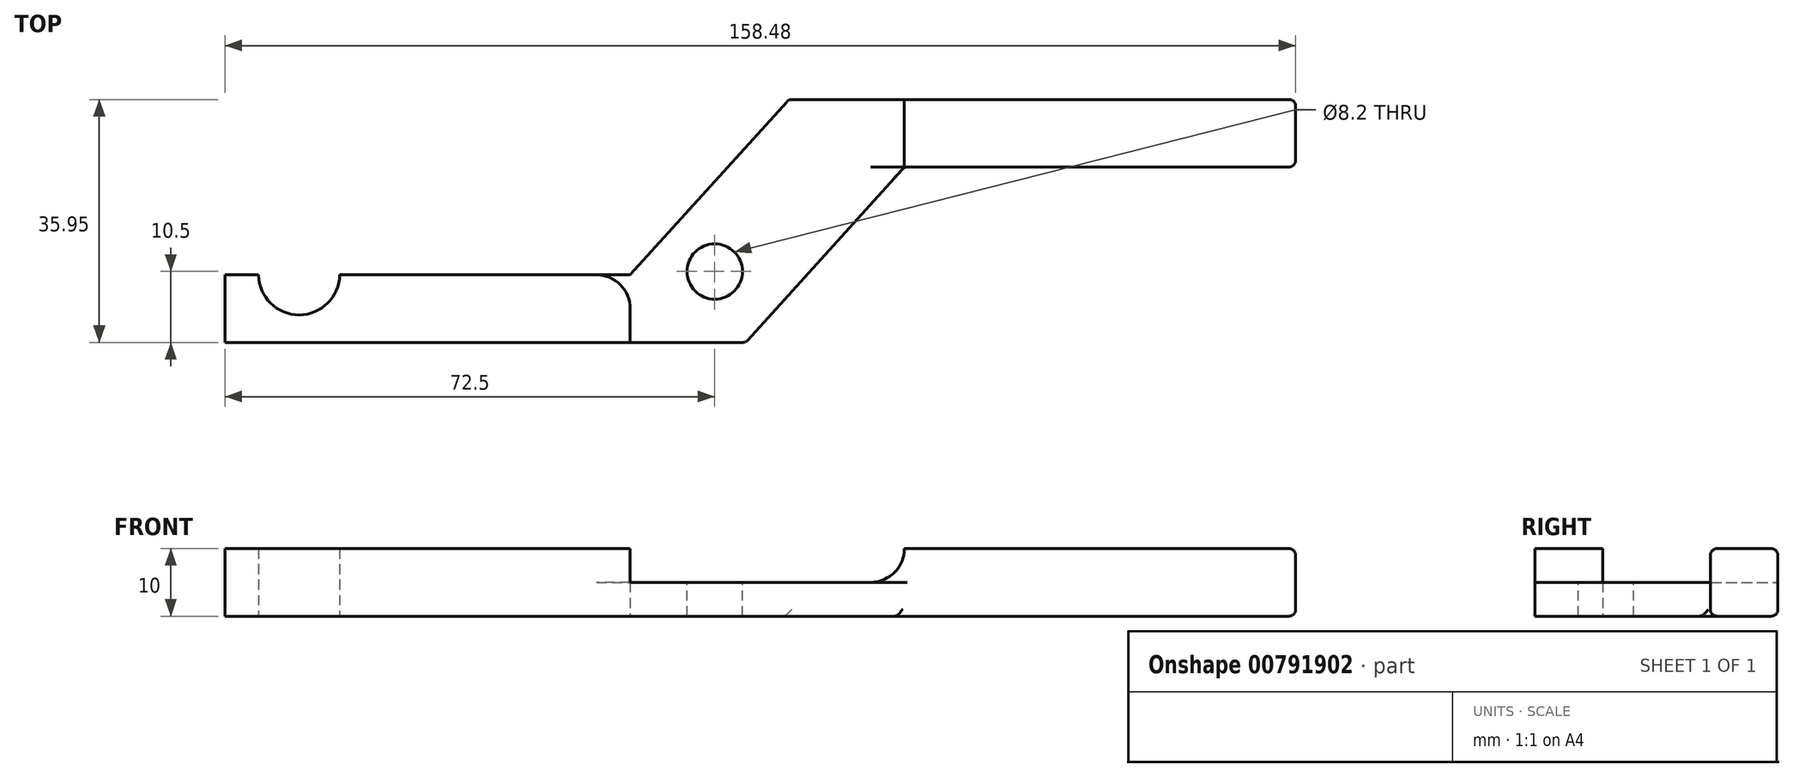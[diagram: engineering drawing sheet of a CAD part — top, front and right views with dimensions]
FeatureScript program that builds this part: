
annotation { "Feature Type Name" : "Feature", "Feature Type Description" : "" }
export const myFeature = defineFeature(function(context is Context, id is Id, definition is map)
    precondition{}
    {
        {
            var Q0;
            Q0=qCreatedBy(makeId("Top.planeOp"),FACE);
            var sketch = newSketch(context, id + "F0", { "sketchPlane" : qUnion([Q0])});
            skLineSegment(sketch, "E0", {"start": v(0, 0) * mm, "end": v(-43, 0) * mm});
            skLineSegment(sketch, "E1", {"start": v(0, 0) * mm, "end": v(23.48, 25.95) * mm});
            skLineSegment(sketch, "E2", {"start": v(23.48, 25.95) * mm, "end": v(98.48, 25.95) * mm});
            skArc(sketch, "E3", {"start": v(-55, 0) * mm, "mid": v(-49, -5.92) * mm, "end": v(-43, 0) * mm});
            skLineSegment(sketch, "E4", {"start": v(-60, 0) * mm, "end": v(-60, -10) * mm});
            skLineSegment(sketch, "E5", {"start": v(-60, -10) * mm, "end": v(17.09, -10) * mm});
            skLineSegment(sketch, "E6", {"start": v(17.09, -10) * mm, "end": v(40.57, 15.95) * mm});
            skLineSegment(sketch, "E7", {"start": v(40.57, 15.95) * mm, "end": v(98.48, 15.95) * mm});
            skLineSegment(sketch, "E8", {"start": v(98.48, 15.95) * mm, "end": v(98.48, 25.95) * mm});
            skLineSegment(sketch, "E9.trimOffspring", {"start": v(-55, 0) * mm, "end": v(-60, 0) * mm});
            skSolve(sketch);
        }
        {
            var Q0;
            Q0=qSketchRegion(id+"F0",true);
            extrude(context, id + "F1", {"entities" : qUnion([Q0]), "depth" : 10 * mm, "offsetDistance" : 25 * mm});
        }
        {
            var Q0;
            Q0=makeQuery(id+"F1.opExtrude","CAP_FACE",FACE,{"disambiguationData":[OSD([sQuery(id+"F0.wireOp",EDGE,"E0"),sQuery(id+"F0.wireOp",EDGE,"E1"),sQuery(id+"F0.wireOp",EDGE,"E2"),sQuery(id+"F0.wireOp",EDGE,"E3"),sQuery(id+"F0.wireOp",EDGE,"E4"),sQuery(id+"F0.wireOp",EDGE,"E5"),sQuery(id+"F0.wireOp",EDGE,"E6"),sQuery(id+"F0.wireOp",EDGE,"E7"),sQuery(id+"F0.wireOp",EDGE,"E8"),sQuery(id+"F0.wireOp",EDGE,"E9.trimOffspring")])],"isStart":false});
            var sketch = newSketch(context, id + "F2", { "sketchPlane" : qUnion([Q0])});
            skLineSegment(sketch, "E10", {"start": v(17.09, -10) * mm, "end": v(40.57, 15.95) * mm});
            skLineSegment(sketch, "E11", {"start": v(23.48, 25.95) * mm, "end": v(0, 0) * mm});
            skCircle(sketch, "E12", {"center": v(12.5, 0.5) * mm, "radius": 4.1 * mm});
            skLineSegment(sketch, "E13", {"start": v(0, 0) * mm, "end": v(0, -10) * mm});
            skLineSegment(sketch, "E14", {"start": v(0, -10) * mm, "end": v(17.09, -10) * mm});
            skLineSegment(sketch, "E15", {"start": v(40.57, 15.95) * mm, "end": v(40.57, 25.95) * mm});
            skLineSegment(sketch, "E16", {"start": v(40.57, 25.95) * mm, "end": v(23.48, 25.95) * mm});
            skSolve(sketch);
        }
        {
            var Q0;
            Q0 = qSketchRegion(id + "F2", true);
            extrude(context, id + "F3", {"entities" : qUnion([Q0]), "operationType" : NewBodyOperationType.REMOVE, "oppositeDirection" : true, "depth" : 5 * mm, "offsetDistance" : 25 * mm});
        }
        {
            var Q0;
            Q0=makeQuery(id+"F3.boolean.opBoolean","SPLIT",FACE,{"disambiguationData":[TD([makeQuery(id+"F3.opExtrude","SWEPT_FACE",FACE,{"disambiguationData":[OSD([sQuery(id+"F2.wireOp",EDGE,"E12")])]})])],"derivedFrom":makeQuery(id+"F1.opExtrude","CAP_FACE",FACE,{"disambiguationData":[OSD([sQuery(id+"F0.wireOp",EDGE,"E0"),sQuery(id+"F0.wireOp",EDGE,"E1"),sQuery(id+"F0.wireOp",EDGE,"E2"),sQuery(id+"F0.wireOp",EDGE,"E3"),sQuery(id+"F0.wireOp",EDGE,"E4"),sQuery(id+"F0.wireOp",EDGE,"E5"),sQuery(id+"F0.wireOp",EDGE,"E6"),sQuery(id+"F0.wireOp",EDGE,"E7"),sQuery(id+"F0.wireOp",EDGE,"E8"),sQuery(id+"F0.wireOp",EDGE,"E9.trimOffspring")])],"isStart":false})});
            var Q1;
            Q1=makeQuery(id+"F1.opExtrude","CAP_FACE",FACE,{"disambiguationData":[OSD([sQuery(id+"F0.wireOp",EDGE,"E0"),sQuery(id+"F0.wireOp",EDGE,"E1"),sQuery(id+"F0.wireOp",EDGE,"E2"),sQuery(id+"F0.wireOp",EDGE,"E3"),sQuery(id+"F0.wireOp",EDGE,"E4"),sQuery(id+"F0.wireOp",EDGE,"E5"),sQuery(id+"F0.wireOp",EDGE,"E6"),sQuery(id+"F0.wireOp",EDGE,"E7"),sQuery(id+"F0.wireOp",EDGE,"E8"),sQuery(id+"F0.wireOp",EDGE,"E9.trimOffspring")])],"isStart":true});
            extrude(context, id + "F4", {"entities" : qUnion([Q0]), "operationType" : NewBodyOperationType.REMOVE, "endBound" : BoundingType.UP_TO_SURFACE, "oppositeDirection" : true, "depth" : 25 * mm, "endBoundEntityFace" : qUnion([Q1]), "offsetDistance" : 25 * mm});
        }
        {
            var Q0;
            Q0=makeQuery(id+"F1.opExtrude","CAP_EDGE",EDGE,{"disambiguationData":[OSD([sQuery(id+"F0.wireOp",EDGE,"E2")])],"isStart":true});
            var Q1;
            Q1=makeQuery(id+"F1.opExtrude","CAP_EDGE",EDGE,{"disambiguationData":[OSD([sQuery(id+"F0.wireOp",EDGE,"E2")])],"isStart":false});
            var Q2;
            Q2=makeQuery(id+"F1.opExtrude","SWEPT_EDGE",EDGE,{"disambiguationData":[OSD([sQuery(id+"F0.wireOp",EDGE,"E2"),sQuery(id+"F0.wireOp",EDGE,"E8")])]});
            var Q3;
            Q3=makeQuery(id+"F1.opExtrude","CAP_EDGE",EDGE,{"disambiguationData":[OSD([sQuery(id+"F0.wireOp",EDGE,"E8")])],"isStart":true});
            var Q4;
            Q4=makeQuery(id+"F1.opExtrude","CAP_EDGE",EDGE,{"disambiguationData":[OSD([sQuery(id+"F0.wireOp",EDGE,"E8")])],"isStart":false});
            var Q5;
            Q5=makeQuery(id+"F1.opExtrude","SWEPT_EDGE",EDGE,{"disambiguationData":[OSD([sQuery(id+"F0.wireOp",EDGE,"E7"),sQuery(id+"F0.wireOp",EDGE,"E8")])]});
            var Q6;
            Q6=makeQuery(id+"F1.opExtrude","CAP_EDGE",EDGE,{"disambiguationData":[OSD([sQuery(id+"F0.wireOp",EDGE,"E7")])],"isStart":true});
            var Q7;
            Q7=makeQuery(id+"F1.opExtrude","CAP_EDGE",EDGE,{"disambiguationData":[OSD([sQuery(id+"F0.wireOp",EDGE,"E7")])],"isStart":false});
            var Q8;
            Q8=makeQuery(id+"F1.opExtrude","SWEPT_EDGE",EDGE,{"disambiguationData":[OSD([sQuery(id+"F0.wireOp",EDGE,"E1"),sQuery(id+"F0.wireOp",EDGE,"E2")])]});
            var Q9;
            Q9=makeQuery(id+"F1.opExtrude","SWEPT_EDGE",EDGE,{"disambiguationData":[OSD([sQuery(id+"F0.wireOp",EDGE,"E5"),sQuery(id+"F0.wireOp",EDGE,"E6")])]});
            var Q10;
            Q10=makeQuery(id+"F3.boolean.opBoolean","SPLIT",EDGE,{"derivedFrom":makeQuery(id+"F1.opExtrude","SWEPT_EDGE",EDGE,{"disambiguationData":[OSD([sQuery(id+"F0.wireOp",EDGE,"E6"),sQuery(id+"F0.wireOp",EDGE,"E7")])]})});
            fillet(context, id + "F5", {"entities" : qUnion([Q0, Q1, Q2, Q3, Q4, Q5, Q6, Q7, Q8, Q9, Q10]), "radius" : 1 * mm, "tangentPropagation" : true, "allowEdgeOverflow" : false});
        }
        {
            var Q0;
            Q0=makeQuery(id+"F3.boolean.opBoolean","COPY",EDGE,{"derivedFrom":makeQuery(id+"F3.opExtrude","CAP_EDGE",EDGE,{"disambiguationData":[OSD([sQuery(id+"F2.wireOp",EDGE,"E15")])],"isStart":false})});
            fillet(context, id + "F6", {"entities" : qUnion([Q0]), "radius" : 5 * mm, "tangentPropagation" : true, "allowEdgeOverflow" : false});
        }
        {
            var Q0;
            {var subQ0=sQuery(id+"F0.wireOp",EDGE,"E0");Q0=makeQuery(id+"F3.boolean.opBoolean","MERGE",EDGE,{"derivedFrom":[makeQuery(id+"F1.opExtrude","SWEPT_EDGE",EDGE,{"disambiguationData":[OSD([subQ0,sQuery(id+"F0.wireOp",EDGE,"E1")])]}),makeQuery(id+"F3.opExtrude","SWEPT_EDGE",EDGE,{"disambiguationData":[OSD([subQ0,sQuery(id+"F2.wireOp",EDGE,"E11"),sQuery(id+"F2.wireOp",EDGE,"E13")])]})]});}
            fillet(context, id + "F7", {"entities" : qUnion([Q0]), "radius" : 5 * mm, "tangentPropagation" : true, "allowEdgeOverflow" : false});
        }
    });
